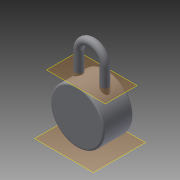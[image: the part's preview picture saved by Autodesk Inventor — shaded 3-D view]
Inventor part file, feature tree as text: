
AUTODESK INVENTOR PART (.ipt)
format: ipt  version: 2015 SP2 (Build 190223200, 223)  size: 1,183,232 bytes
history: native  units: mm
features: sketch x9, extrude x6, fillet x4, other x3, plane x2, revolve x1
ambient origin geometry x8: Origin, YZ Plane, XZ Plane, XY Plane, X Axis, Y Axis, Z Axis, Center Point
bodies: Solid1 (feature_tree)
feature tree (25):
  extrude  "Extrusion1"  Depth=29.57mm TaperAngle=0.0deg
  sketch  "Sketch2"  dims[d3=34.7mm d4=8.0mm]
  plane  "Work Plane1"
  extrude  "Extrusion2"  Depth=8.0mm
  sketch  "Sketch4"  dims[d9=8.0mm d10=90.0deg]
  other  "Work Point1"
  other  "Work Point2"
  other  "Work Axis1"
  revolve  "Revolution1"  [1 undecoded]
  sketch  "Sketch8"  dims[d19=1.5mm d20=1.0mm]
  extrude  "Extrusion3"  TaperAngle=90.0deg  [1 undecoded]
  extrude  "Extrusion4"  Depth=53.5mm
  fillet  "Fillet1"  Radius=0.5mm
  fillet  "Fillet2"  Radius=0.5mm
  fillet  "Fillet3"  Radius=2.0mm
  fillet  "Fillet4"  Radius=1.5mm
  plane  "Work Plane2"
  extrude  "Extrusion5"  Depth=1.0mm
  extrude  "Extrusion6"  Depth=13.0mm
  sketch  "Sketch1"  dims[d0=54.75mm d1=29.57mm d2=0.0mm]
  sketch  "Sketch3"  dims[d5=10.0mm d6=0.0mm d7=18.0mm d8=0.0mm]
  sketch  "Sketch5"  dims[d11=53.5mm d12=53.5mm d13=0.5mm d14=0.0mm d15=0.5mm d16=0.0mm d17=2.0mm d18=1.5mm]
  sketch  "Sketch9"  dims[d21=15.0mm d22=13.0mm]
  sketch  "Sketch10"  dims[d23=0.5mm d24=0.0mm]
  sketch  "Sketch11"  dims[d25=1.0mm d26=0.0mm]
note: 2 required parameter values undecoded (feature->parameter linkage not recoverable at this tier; creation-order binding heuristic only, values carry confidence <= 0.55)